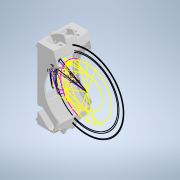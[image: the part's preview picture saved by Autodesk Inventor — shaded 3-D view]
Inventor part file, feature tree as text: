
AUTODESK INVENTOR PART (.ipt)
format: ipt  version: 2022 (Build 260153000, 153)  size: 1,238,528 bytes
history: native  units: mm
features: reference x76, other x25, sketch x24, projected_geometry x22, extrude x21, fillet x15, mirror x5, revolve x2, chamfer x2
ambient origin geometry x8: Origin, YZ Plane, XZ Plane, XY Plane, X Axis, Y Axis, Z Axis, Center Point
bodies: Body1 (feature_tree)
feature tree (192):
  other  "Твердое тело1"
  sketch  "Эскиз1"
  extrude  "Выдавливание1"  Depth=3.490659mm
  extrude  "Выдавливание2"  Depth=3.490659mm
  extrude  "Выдавливание3"  Depth=1.0mm
  sketch  "Эскиз5"
  extrude  "Выдавливание4"  Depth=1.0mm
  extrude  "Выдавливание5"  Depth=4.537856mm
  other  "РабПлоскость1"
  extrude  "Выдавливание6"  Depth=4.537856mm
  extrude  "Выдавливание7"  Depth=0.5mm
  extrude  "Выдавливание8"  Depth=18.69mm TaperAngle=0.0deg
  fillet  "Сопряжение2"  Radius=20.45mm
  extrude  "Выдавливание9"  Depth=1.5mm TaperAngle=0.0deg
  extrude  "Выдавливание10"  Depth=1.5mm
  fillet  "Сопряжение3"  Radius=3.0mm
  fillet  "Сопряжение4"  Radius=19.547688mm
  extrude  "Выдавливание11"  Depth=9.773844mm
  fillet  "Сопряжение6"  Radius=2.0mm
  fillet  "Сопряжение7"  Radius=28.843311mm
  extrude  "Выдавливание12"  Depth=1.5mm
  extrude  "Выдавливание13"  Depth=1.2mm
  fillet  "Сопряжение8"  Radius=1.5mm
  revolve  "Вращение1"
  fillet  "Сопряжение9"  Radius=20.69mm
  fillet  "Сопряжение10"  Radius=11.0mm
  extrude  "Выдавливание14"  Depth=1.3mm
  fillet  "Сопряжение11"  Radius=14.5mm
  fillet  "Сопряжение12"  Radius=11.0mm
  fillet  "Сопряжение13"  Radius=9.0mm
  chamfer  "Фаска1"  Distance=9.0mm
  extrude  "Выдавливание15"  Depth=2.0mm
  fillet  "Сопряжение14"  Radius=1.0mm
  extrude  "Выдавливание16"  Depth=0.3mm
  extrude  "Выдавливание17"  Depth=0.3mm
  mirror  "Зеркальное отражение1"
  revolve  "Вращение2"
  extrude  "Выдавливание18"  Depth=0.3mm
  mirror  "Зеркальное отражение2"
  fillet  "Сопряжение17"  Radius=0.3mm
  extrude  "Выдавливание19"  Depth=25.0mm TaperAngle=0.0deg
  extrude  "Выдавливание20"  Depth=0.3mm TaperAngle=0.0deg
  mirror  "Зеркальное отражение3"
  mirror  "Зеркальное отражение4"
  fillet  "Сопряжение18"  Radius=2.0mm
  fillet  "Сопряжение19"  Radius=10.0mm
  extrude  "Выдавливание21"  Depth=1.0mm
  mirror  "Зеркальное отражение5"
  chamfer  "Фаска2"  Distance=0.7mm
  reference  "Ссылка1"
  reference  "Ссылка2"
  reference  "Ссылка3"
  reference  "Ссылка4"
  reference  "Ссылка5"
  reference  "Ссылка6"
  reference  "Ссылка7"
  reference  "Ссылка8"
  reference  "Ссылка9"
  reference  "Ссылка10"
  reference  "Ссылка11"
  reference  "Ссылка12"
  reference  "Ссылка13"
  reference  "Ссылка14"
  reference  "Ссылка15"
  reference  "Ссылка16"
  reference  "Ссылка17"
  reference  "Ссылка18"
  reference  "Ссылка19"
  reference  "Ссылка20"
  reference  "Ссылка21"
  reference  "Ссылка22"
  reference  "Ссылка23"
  reference  "Ссылка24"
  reference  "Ссылка25"
  sketch  "Эскиз2"
  reference  "Ссылка26"
  reference  "Ссылка27"
  reference  "Ссылка28"
  reference  "Ссылка29"
  reference  "Ссылка30"
  sketch  "Эскиз3"
  projected_geometry  "Спроецированная петля1"
  projected_geometry  "Спроецированная петля2"
  reference  "Ссылка31"
  sketch  "Эскиз4"
  projected_geometry  "Спроецированная петля3"
  reference  "Ссылка32"
  projected_geometry  "Спроецированная петля4"
  projected_geometry  "Спроецированная петля5"
  reference  "Ссылка33"
  reference  "Ссылка34"
  reference  "Ссылка35"
  reference  "Ссылка47"
  sketch  "Эскиз6"
  projected_geometry  "Спроецированная петля6"
  sketch  "Эскиз7"
  projected_geometry  "Спроецированная петля7"
  sketch  "Эскиз8"
  reference  "Ссылка51"
  projected_geometry  "Спроецированная петля8"
  sketch  "Эскиз10"
  reference  "Ссылка54"
  reference  "Ссылка55"
  reference  "Ссылка56"
  reference  "Ссылка57"
  reference  "Ссылка58"
  sketch  "Эскиз11"
  projected_geometry  "Спроецированная петля9"
  sketch  "Эскиз12"
  projected_geometry  "Спроецированная петля10"
  reference  "Ссылка59"
  reference  "Ссылка60"
  reference  "Ссылка61"
  sketch  "Эскиз13"
  reference  "Ссылка62"
  reference  "Ссылка63"
  reference  "Ссылка64"
  reference  "Ссылка65"
  sketch  "Эскиз14"
  reference  "Ссылка66"
  projected_geometry  "Спроецированная петля11"
  sketch  "Эскиз15"
  projected_geometry  "Спроецированная петля12"
  sketch  "Эскиз16"
  reference  "Ссылка67"
  reference  "Ссылка68"
  reference  "Ссылка69"
  reference  "Ссылка70"
  reference  "Ссылка71"
  reference  "Ссылка72"
  sketch  "Эскиз17"
  reference  "Ссылка73"
  reference  "Ссылка74"
  projected_geometry  "Спроецированная петля13"
  projected_geometry  "Спроецированная петля14"
  reference  "Ссылка75"
  reference  "Ссылка76"
  sketch  "Эскиз18"
  reference  "Ссылка77"
  reference  "Ссылка78"
  reference  "Ссылка79"
  reference  "Ссылка80"
  reference  "Ссылка81"
  reference  "Ссылка82"
  reference  "Ссылка83"
  reference  "Ссылка84"
  sketch  "Эскиз19"
  reference  "Ссылка85"
  reference  "Ссылка86"
  projected_geometry  "Спроецированная петля15"
  projected_geometry  "Спроецированная петля16"
  projected_geometry  "Спроецированная петля17"
  sketch  "Эскиз20"
  reference  "Ссылка87"
  reference  "Ссылка88"
  reference  "Ссылка89"
  sketch  "Эскиз21"
  sketch  "Эскиз22"
  projected_geometry  "Спроецированная петля18"
  sketch  "Эскиз23"
  reference  "Ссылка90"
  projected_geometry  "Спроецированная петля19"
  sketch  "Эскиз24"
  projected_geometry  "Спроецированная петля20"
  sketch  "Эскиз25"
  projected_geometry  "Спроецированная петля21"
  projected_geometry  "Спроецированная петля22"
  reference  "Ссылка91"
  reference  "Ссылка92"
  other  "<userpath>\Documents\Git\MZCAT_2024\MZCAT_2.iam"
  other  "MZCAT_2.iam"
  other  "lidar_krestovina:1"
  other  "shatun_lidar:1"
  other  "stabilisator_plan:1"
  other  "OCS-D008 B:3"
  other  "commutationCATboard:1"
  other  "CAT_protector:1"
  other  "OCS-D008 B:2"
  other  "<userpath>\Documents\Git\MZCAT_2024\MZCAT_4.iam"
  other  "MZCAT_4.iam"
  other  "vydacha_pusher:2"
  other  "FastBattery:1"
  other  "metal_cap:1"
  other  "base plate:1"
  other  "base plate:2"
  other  "<userpath>\Documents\Git\MZCAT_2024\MZCAT_3.iam"
  other  "MZCAT_3.iam"
  other  "akkum_cup:1"
  other  "vydacha_slide:1"
  other  "camera:3"
  other  "camera:4"
  other  "shelka_lidar:1"
